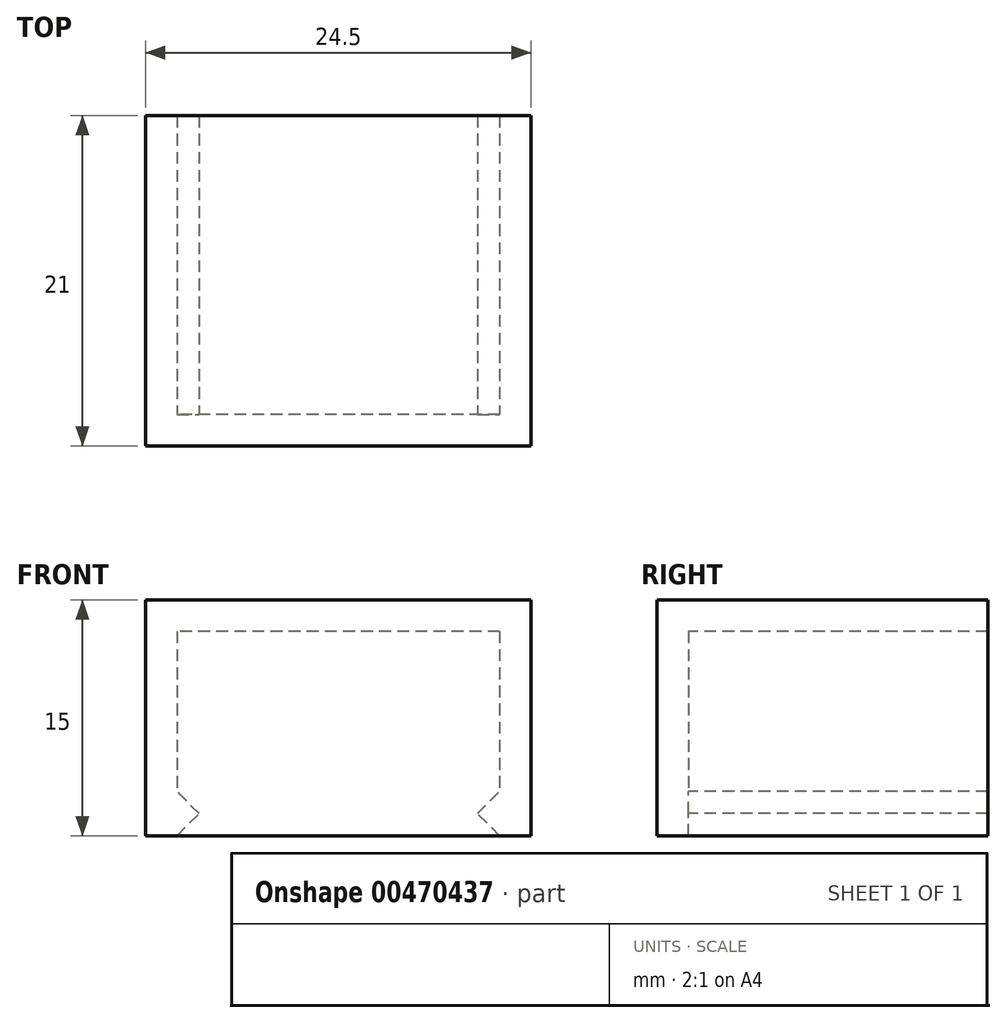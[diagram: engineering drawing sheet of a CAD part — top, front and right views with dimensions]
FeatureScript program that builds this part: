
annotation { "Feature Type Name" : "Feature", "Feature Type Description" : "" }
export const myFeature = defineFeature(function(context is Context, id is Id, definition is map)
    precondition{}
    {
        {
            var Q0;
            Q0=qCreatedBy(makeId("Top.planeOp"),FACE);
            var sketch = newSketch(context, id + "F0", { "sketchPlane" : qUnion([Q0])});
            skLineSegment(sketch, "E0.bottom", {"start": v(12.25, 10.5) * mm, "end": v(-12.25, 10.5) * mm});
            skLineSegment(sketch, "E0.top", {"start": v(12.25, -10.5) * mm, "end": v(-12.25, -10.5) * mm});
            skLineSegment(sketch, "E0.left", {"start": v(12.25, 10.5) * mm, "end": v(12.25, -10.5) * mm});
            skLineSegment(sketch, "E0.right", {"start": v(-12.25, 10.5) * mm, "end": v(-12.25, -10.5) * mm});
            skPoint(sketch, "E0.middle", {"position": v(0, 0) * mm});
            skSolve(sketch);
        }
        {
            var Q0;
            Q0=makeQuery(id+"F0.imprint","IMPRINT",FACE,{"disambiguationData":[TD([[makeQuery(id+"F0.imprint","IMPRINT",EDGE,{"derivedFrom":sQuery(id+"F0.wireOp",EDGE,"E0.bottom")}),1.0]])]});
            extrude(context, id + "F1", {"entities" : qUnion([Q0]), "depth" : 15 * mm, "offsetDistance" : 25 * mm});
        }
        {
            var Q0;
            Q0=makeQuery(id+"F1.opExtrude","CAP_FACE",FACE,{"disambiguationData":[OSD([sQuery(id+"F0.wireOp",EDGE,"E0.bottom"),sQuery(id+"F0.wireOp",EDGE,"E0.top"),sQuery(id+"F0.wireOp",EDGE,"E0.left"),sQuery(id+"F0.wireOp",EDGE,"E0.right")])],"isStart":true});
            var Q1;
            Q1=makeQuery(id+"F1.opExtrude","SWEPT_FACE",FACE,{"disambiguationData":[OSD([sQuery(id+"F0.wireOp",EDGE,"E0.bottom")])]});
            shell(context, id + "F2", {"entities" : qUnion([Q0, Q1]), "thickness" : 2 * mm});
        }
        {
            var Q0;
            Q0=makeQuery(id+"F2.opShell","OFFSET_FACE",FACE,{"disambiguationData":[OSD([sQuery(id+"F0.wireOp",EDGE,"E0.top")])]});
            var sketch = newSketch(context, id + "F3", { "sketchPlane" : qUnion([Q0])});
            skLineSegment(sketch, "E1", {"start": v(-10.25, 0) * mm, "end": v(-8.84, 1.41) * mm});
            skLineSegment(sketch, "E2", {"start": v(-8.84, 1.41) * mm, "end": v(-10.25, 2.83) * mm});
            skLineSegment(sketch, "E3.MirrorCS", {"start": v(8.84, 1.41) * mm, "end": v(10.25, 2.83) * mm});
            skLineSegment(sketch, "E4.MirrorCS", {"start": v(10.25, 0) * mm, "end": v(8.84, 1.41) * mm});
            skSolve(sketch);
        }
        {
            var Q0;
            {var subQ0=sQuery(id+"F3.wireOp",EDGE,"E1");Q0=makeQuery(id+"F3.imprint","IMPRINT",FACE,{"disambiguationData":[TD([[makeQuery(id+"F3.imprint","IMPRINT",EDGE,{"derivedFrom":subQ0}),1.0]])]});}
            var Q1;
            {var subQ0=sQuery(id+"F3.wireOp",EDGE,"E3.MirrorCS");Q1=makeQuery(id+"F3.imprint","IMPRINT",FACE,{"disambiguationData":[TD([[makeQuery(id+"F3.imprint","IMPRINT",EDGE,{"derivedFrom":subQ0}),-1.0]])]});}
            var Q2;
            Q2=makeQuery(id+"F2.opShell","OFFSET_FACE",FACE,{"disambiguationData":[OSD([sQuery(id+"F0.wireOp",EDGE,"E0.right")])]});
            var Q3;
            Q3=makeQuery(id+"F1.opExtrude","SWEPT_BODY",BODY,{"disambiguationData":[OSD([sQuery(id+"F0.wireOp",EDGE,"E0.bottom"),sQuery(id+"F0.wireOp",EDGE,"E0.top"),sQuery(id+"F0.wireOp",EDGE,"E0.left"),sQuery(id+"F0.wireOp",EDGE,"E0.right")])]});
            extrude(context, id + "F4", {"entities" : qUnion([Q0, Q1]), "operationType" : NewBodyOperationType.ADD, "depth" : 19 * mm, "endBoundEntityFace" : qUnion([Q2]), "endBoundEntityBody" : qUnion([Q3]), "offsetDistance" : 25 * mm});
        }
    });
